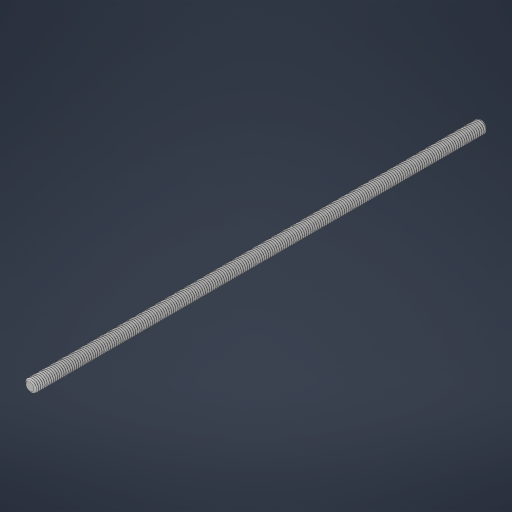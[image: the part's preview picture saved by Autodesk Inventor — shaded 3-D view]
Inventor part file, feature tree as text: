
AUTODESK INVENTOR PART (.ipt)
format: ipt  version: 2023 (Build 270158000, 158)  size: 3,466,240 bytes
history: native  units: in
note: dims shown in document units (in); Inventor stores cm internally (conversion verified against a paired STEP export)
features: mirror x1
ambient origin geometry x8: Origin, YZ Plane, XZ Plane, XY Plane, X Axis, Y Axis, Z Axis, Center Point
bodies: Solid1 (feature_tree)
feature tree (1):
  mirror  "Mirror1"
